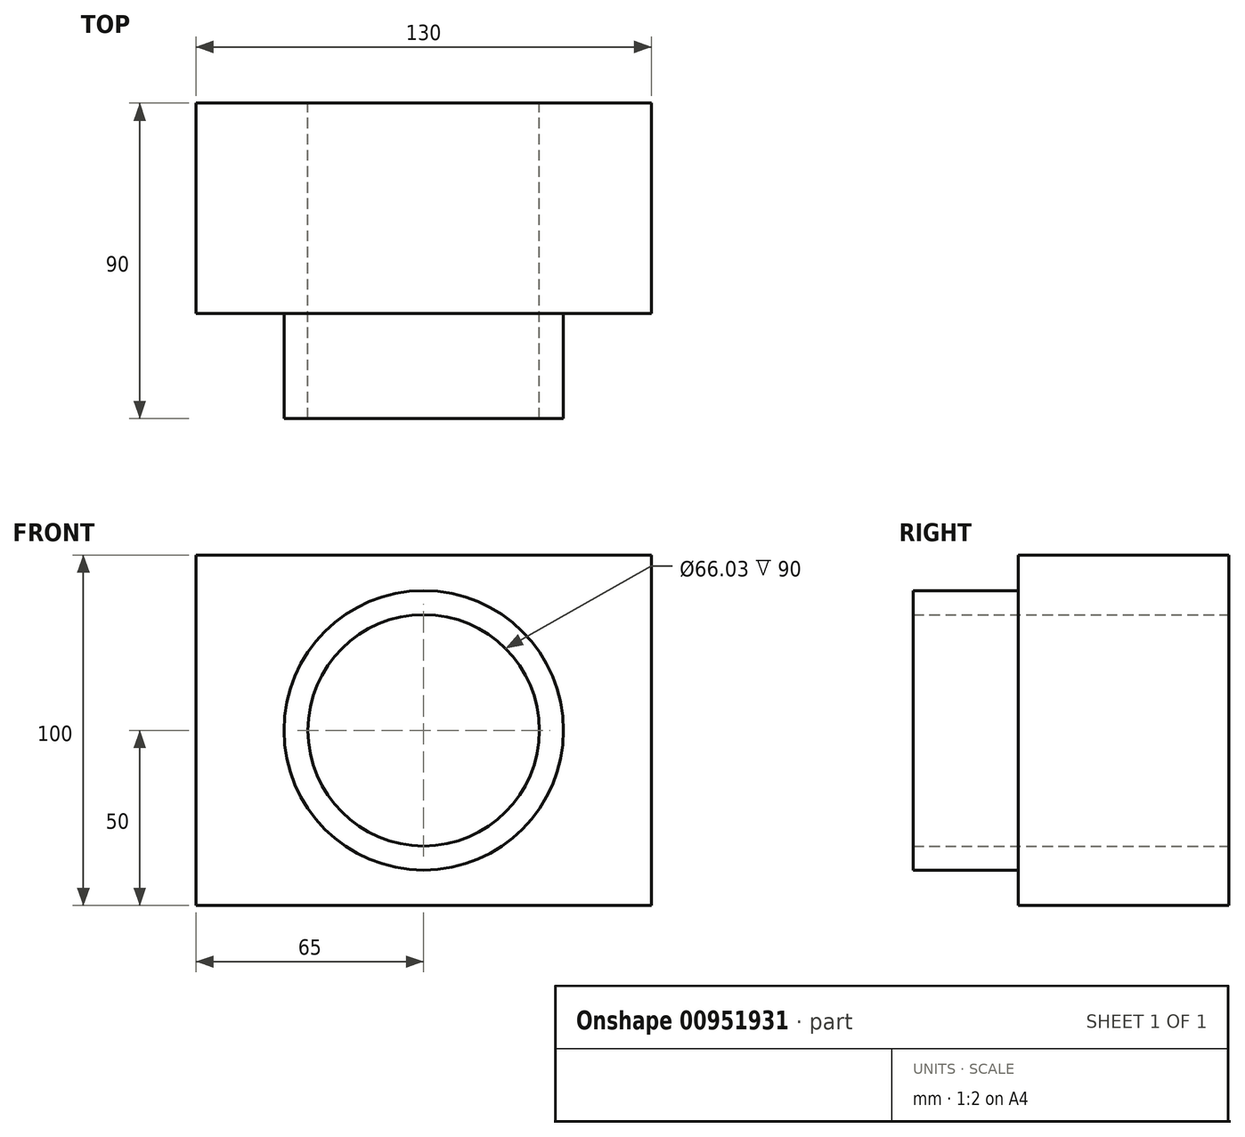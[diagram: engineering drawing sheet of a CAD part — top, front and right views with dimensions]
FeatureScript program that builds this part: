
annotation { "Feature Type Name" : "Feature", "Feature Type Description" : "" }
export const myFeature = defineFeature(function(context is Context, id is Id, definition is map)
    precondition{}
    {
        {
            var Q0;
            Q0=qCreatedBy(makeId("Front.planeOp"),FACE);
            var sketch = newSketch(context, id + "F0", { "sketchPlane" : qUnion([Q0])});
            skLineSegment(sketch, "E0.bottom", {"start": v(-65, 50) * mm, "end": v(65, 50) * mm});
            skLineSegment(sketch, "E0.top", {"start": v(-65, -50) * mm, "end": v(65, -50) * mm});
            skLineSegment(sketch, "E0.left", {"start": v(-65, 50) * mm, "end": v(-65, -50) * mm});
            skLineSegment(sketch, "E0.right", {"start": v(65, 50) * mm, "end": v(65, -50) * mm});
            skSolve(sketch);
        }
        {
            var Q0;
            Q0=makeQuery(id+"F0.imprint","IMPRINT",FACE,{"disambiguationData":[TD([[makeQuery(id+"F0.imprint","IMPRINT",EDGE,{"derivedFrom":sQuery(id+"F0.wireOp",EDGE,"E0.bottom")}),-1.0]])]});
            extrude(context, id + "F1", {"entities" : qUnion([Q0]), "depth" : 30 * mm, "offsetDistance" : 25 * mm});
        }
        {
            var Q0;
            Q0=makeQuery(id+"F1.opExtrude","CAP_FACE",FACE,{"disambiguationData":[OSD([sQuery(id+"F0.wireOp",EDGE,"E0.bottom"),sQuery(id+"F0.wireOp",EDGE,"E0.top"),sQuery(id+"F0.wireOp",EDGE,"E0.left"),sQuery(id+"F0.wireOp",EDGE,"E0.right")])],"isStart":true});
            extrude(context, id + "F2", {"entities" : qUnion([Q0]), "operationType" : NewBodyOperationType.ADD, "depth" : 30 * mm, "offsetDistance" : 25 * mm});
        }
        {
            var Q0;
            Q0=makeQuery(id+"F1.opExtrude","CAP_FACE",FACE,{"disambiguationData":[OSD([sQuery(id+"F0.wireOp",EDGE,"E0.bottom"),sQuery(id+"F0.wireOp",EDGE,"E0.top"),sQuery(id+"F0.wireOp",EDGE,"E0.left"),sQuery(id+"F0.wireOp",EDGE,"E0.right")])],"isStart":false});
            var sketch = newSketch(context, id + "F3", { "sketchPlane" : qUnion([Q0])});
            skCircle(sketch, "E1", {"center": v(0, 0) * mm, "radius": 33.01 * mm});
            skCircle(sketch, "E2", {"center": v(0, 0) * mm, "radius": 39.86 * mm});
            skSolve(sketch);
        }
        {
            var Q0;
            Q0=makeQuery(id+"F3.imprint","IMPRINT",FACE,{"disambiguationData":[TD([[makeQuery(id+"F3.imprint","IMPRINT",EDGE,{"derivedFrom":sQuery(id+"F3.wireOp",EDGE,"E1")}),-1.0]])]});
            extrude(context, id + "F4", {"entities" : qUnion([Q0]), "operationType" : NewBodyOperationType.ADD, "depth" : 30 * mm, "offsetDistance" : 25 * mm});
        }
        {
            var Q0;
            Q0=makeQuery(id+"F4.boolean.opBoolean","SPLIT",FACE,{"disambiguationData":[TD([makeQuery(id+"F4.opExtrude","SWEPT_FACE",FACE,{"disambiguationData":[OSD([sQuery(id+"F3.wireOp",EDGE,"E1")])]})])],"derivedFrom":makeQuery(id+"F1.opExtrude","CAP_FACE",FACE,{"disambiguationData":[OSD([sQuery(id+"F0.wireOp",EDGE,"E0.bottom"),sQuery(id+"F0.wireOp",EDGE,"E0.top"),sQuery(id+"F0.wireOp",EDGE,"E0.left"),sQuery(id+"F0.wireOp",EDGE,"E0.right")])],"isStart":false})});
            extrude(context, id + "F5", {"entities" : qUnion([Q0]), "operationType" : NewBodyOperationType.REMOVE, "oppositeDirection" : true, "depth" : 60 * mm, "offsetDistance" : 25 * mm});
        }
    });
